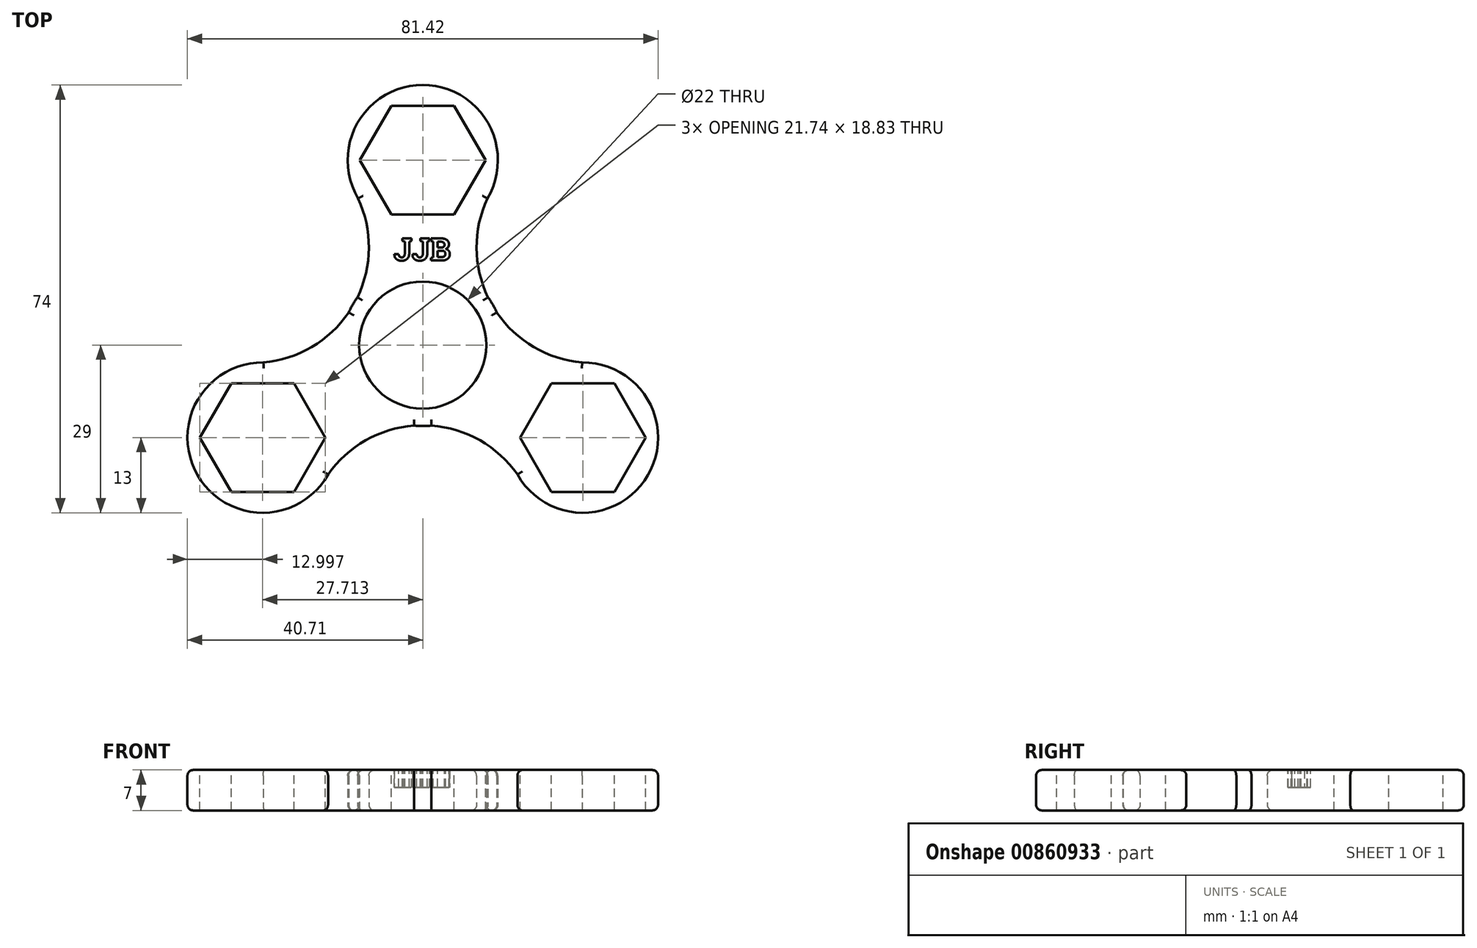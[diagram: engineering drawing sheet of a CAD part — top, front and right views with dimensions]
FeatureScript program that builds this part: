
annotation { "Feature Type Name" : "Feature", "Feature Type Description" : "" }
export const myFeature = defineFeature(function(context is Context, id is Id, definition is map)
    precondition{}
    {
        {
            var Q0;
            Q0=qCreatedBy(makeId("Top.planeOp"),FACE);
            var sketch = newSketch(context, id + "F0", { "sketchPlane" : qUnion([Q0])});
            skCircle(sketch, "E0", {"center": v(0, 0) * mm, "radius": 11 * mm});
            skCircle(sketch, "E1.0", {"center": v(0, 0) * mm, "radius": 14 * mm});
            skCircle(sketch, "E2", {"center": v(0, 0) * mm, "radius": 45 * mm, "construction": true});
            skArc(sketch, "E3", {"start": v(11.19, 25.38) * mm, "mid": v(0, 45) * mm, "end": v(-11.19, 25.38) * mm});
            skArc(sketch, "E4", {"start": v(-11.3, 8.27) * mm, "mid": v(-9.32, 16.81) * mm, "end": v(-11.19, 25.38) * mm});
            skArc(sketch, "E5.MirrorCS", {"start": v(11.3, 8.27) * mm, "mid": v(9.32, 16.81) * mm, "end": v(11.19, 25.38) * mm});
            skArc(sketch, "E6.1.0", {"start": v(-27.57, -3) * mm, "mid": v(-38.97, -22.5) * mm, "end": v(-16.39, -22.38) * mm});
            skArc(sketch, "E6.1.1", {"start": v(-1.52, -13.92) * mm, "mid": v(-9.9, -16.48) * mm, "end": v(-16.39, -22.38) * mm});
            skArc(sketch, "E6.1.2", {"start": v(-12.81, 5.65) * mm, "mid": v(-19.22, -0.34) * mm, "end": v(-27.57, -3) * mm});
            skArc(sketch, "E6.2.0", {"start": v(16.39, -22.38) * mm, "mid": v(38.97, -22.5) * mm, "end": v(27.57, -3) * mm});
            skArc(sketch, "E6.2.1", {"start": v(12.81, 5.65) * mm, "mid": v(19.22, -0.34) * mm, "end": v(27.57, -3) * mm});
            skArc(sketch, "E6.2.2", {"start": v(1.52, -13.92) * mm, "mid": v(9.9, -16.48) * mm, "end": v(16.39, -22.38) * mm});
            skText(sketch, "E7", { "text": "JJB", "fontName": "RobotoSlab-Bold.ttf"});
            const initialGuessF0  = {"E7": [-0.005, 0.0162, 1, 0, 0.00387]};
            skSetInitialGuess(sketch, initialGuessF0);
            skSolve(sketch);
        }
        {
            var Q0;
            {var subQ0=sQuery(id+"F0.wireOp",EDGE,"E4");Q0=makeQuery(id+"F0.imprint","IMPRINT",FACE,{"disambiguationData":[TD([[makeQuery(id+"F0.imprint","IMPRINT",EDGE,{"derivedFrom":subQ0}),-1.0]])]});}
            var Q1;
            {var subQ0=sQuery(id+"F0.wireOp",EDGE,"E3");var subQ1=makeQuery(id+"F0.imprint","INTERSECT",VERTEX,{"derivedFrom":[subQ0,sQuery(id+"F0.wireOp",EDGE,"E4")]});Q1=makeQuery(id+"F0.imprint","IMPRINT",FACE,{"disambiguationData":[TD([[makeQuery(id+"F0.imprint","IMPRINT",EDGE,{"disambiguationData":[TD([[subQ1,-1.0]])],"derivedFrom":subQ0}),1.0]])]});}
            var Q2;
            Q2=makeQuery(id+"F0.imprint","IMPRINT",FACE,{"disambiguationData":[TD([[makeQuery(id+"F0.imprint","IMPRINT",EDGE,{"derivedFrom":sQuery(id+"F0.wireOp",EDGE,"E0")}),-1.0]])]});
            var Q3;
            {var subQ0=sQuery(id+"F0.wireOp",EDGE,"E6.2.1");Q3=makeQuery(id+"F0.imprint","IMPRINT",FACE,{"disambiguationData":[TD([[makeQuery(id+"F0.imprint","IMPRINT",EDGE,{"derivedFrom":subQ0}),-1.0]])]});}
            var Q4;
            {var subQ0=sQuery(id+"F0.wireOp",EDGE,"E6.1.1");Q4=makeQuery(id+"F0.imprint","IMPRINT",FACE,{"disambiguationData":[TD([[makeQuery(id+"F0.imprint","IMPRINT",EDGE,{"derivedFrom":subQ0}),-1.0]])]});}
            var Q5;
            {var subQ0=sQuery(id+"F0.wireOp",EDGE,"E6.1.0");var subQ1=makeQuery(id+"F0.imprint","INTERSECT",VERTEX,{"derivedFrom":[subQ0,sQuery(id+"F0.wireOp",EDGE,"E6.1.1")]});Q5=makeQuery(id+"F0.imprint","IMPRINT",FACE,{"disambiguationData":[TD([[makeQuery(id+"F0.imprint","IMPRINT",EDGE,{"disambiguationData":[TD([[subQ1,-1.0]])],"derivedFrom":subQ0}),1.0]])]});}
            var Q6;
            {var subQ0=sQuery(id+"F0.wireOp",EDGE,"E6.2.0");var subQ1=makeQuery(id+"F0.imprint","INTERSECT",VERTEX,{"derivedFrom":[subQ0,sQuery(id+"F0.wireOp",EDGE,"E6.2.1")]});Q6=makeQuery(id+"F0.imprint","IMPRINT",FACE,{"disambiguationData":[TD([[makeQuery(id+"F0.imprint","IMPRINT",EDGE,{"disambiguationData":[TD([[subQ1,-1.0]])],"derivedFrom":subQ0}),1.0]])]});}
            var Q7;
            Q7=makeQuery(id+"F0.imprint","IMPRINT",FACE,{"disambiguationData":[TD([[makeQuery(id+"F0.imprint","IMPRINT",EDGE,{"derivedFrom":sQuery(id+"F0.wireOp",EDGE,"E7.sketch_text.stroke-36")}),-1.0]])]});
            var Q8;
            Q8=makeQuery(id+"F0.imprint","IMPRINT",FACE,{"disambiguationData":[TD([[makeQuery(id+"F0.imprint","IMPRINT",EDGE,{"derivedFrom":sQuery(id+"F0.wireOp",EDGE,"E7.sketch_text.stroke-18")}),-1.0]])]});
            var Q9;
            Q9=makeQuery(id+"F0.imprint","IMPRINT",FACE,{"disambiguationData":[TD([[makeQuery(id+"F0.imprint","IMPRINT",EDGE,{"derivedFrom":sQuery(id+"F0.wireOp",EDGE,"E7.sketch_text.stroke-0")}),-1.0]])]});
            var Q10;
            Q10=makeQuery(id+"F0.imprint","IMPRINT",FACE,{"disambiguationData":[TD([[makeQuery(id+"F0.imprint","IMPRINT",EDGE,{"derivedFrom":sQuery(id+"F0.wireOp",EDGE,"E7.sketch_text.stroke-59")}),1.0]])]});
            var Q11;
            Q11=makeQuery(id+"F0.imprint","IMPRINT",FACE,{"disambiguationData":[TD([[makeQuery(id+"F0.imprint","IMPRINT",EDGE,{"derivedFrom":sQuery(id+"F0.wireOp",EDGE,"E7.sketch_text.stroke-52")}),1.0]])]});
            extrude(context, id + "F1", {"entities" : qUnion([Q0, Q1, Q2, Q3, Q4, Q5, Q6, Q7, Q8, Q9, Q10, Q11]), "depth" : 7 * mm, "offsetDistance" : 25 * mm});
        }
        {
            var Q0;
            Q0=makeQuery(id+"F1.opExtrude","CAP_FACE",FACE,{"disambiguationData":[OSD([sQuery(id+"F0.wireOp",EDGE,"E0"),sQuery(id+"F0.wireOp",EDGE,"E1.0"),sQuery(id+"F0.wireOp",EDGE,"E3"),sQuery(id+"F0.wireOp",EDGE,"E4"),sQuery(id+"F0.wireOp",EDGE,"E5.MirrorCS"),sQuery(id+"F0.wireOp",EDGE,"E6.1.0"),sQuery(id+"F0.wireOp",EDGE,"E6.1.1"),sQuery(id+"F0.wireOp",EDGE,"E6.1.2"),sQuery(id+"F0.wireOp",EDGE,"E6.2.0"),sQuery(id+"F0.wireOp",EDGE,"E6.2.1"),sQuery(id+"F0.wireOp",EDGE,"E6.2.2")])],"isStart":true});
            var Q1;
            Q1=makeQuery(id+"F1.opExtrude","CAP_FACE",FACE,{"disambiguationData":[OSD([sQuery(id+"F0.wireOp",EDGE,"E0"),sQuery(id+"F0.wireOp",EDGE,"E1.0"),sQuery(id+"F0.wireOp",EDGE,"E3"),sQuery(id+"F0.wireOp",EDGE,"E4"),sQuery(id+"F0.wireOp",EDGE,"E5.MirrorCS"),sQuery(id+"F0.wireOp",EDGE,"E6.1.0"),sQuery(id+"F0.wireOp",EDGE,"E6.1.1"),sQuery(id+"F0.wireOp",EDGE,"E6.1.2"),sQuery(id+"F0.wireOp",EDGE,"E6.2.0"),sQuery(id+"F0.wireOp",EDGE,"E6.2.1"),sQuery(id+"F0.wireOp",EDGE,"E6.2.2")])],"isStart":false});
            fillet(context, id + "F2", {"entities" : qUnion([Q0, Q1]), "radius" : 1 * mm, "tangentPropagation" : true, "allowEdgeOverflow" : false});
        }
        {
            var Q0;
            Q0=makeQuery(id+"F1.opExtrude","CAP_FACE",FACE,{"disambiguationData":[OSD([sQuery(id+"F0.wireOp",EDGE,"E0"),sQuery(id+"F0.wireOp",EDGE,"E1.0"),sQuery(id+"F0.wireOp",EDGE,"E3"),sQuery(id+"F0.wireOp",EDGE,"E4"),sQuery(id+"F0.wireOp",EDGE,"E5.MirrorCS"),sQuery(id+"F0.wireOp",EDGE,"E6.1.0"),sQuery(id+"F0.wireOp",EDGE,"E6.1.1"),sQuery(id+"F0.wireOp",EDGE,"E6.1.2"),sQuery(id+"F0.wireOp",EDGE,"E6.2.0"),sQuery(id+"F0.wireOp",EDGE,"E6.2.1"),sQuery(id+"F0.wireOp",EDGE,"E6.2.2")])],"isStart":false});
            var sketch = newSketch(context, id + "F3", { "sketchPlane" : qUnion([Q0])});
            skCircle(sketch, "E8.cCircle", {"center": v(0, 32) * mm, "radius": 9.41 * mm, "construction": true});
            skLineSegment(sketch, "E8.0", {"start": v(5.44, 22.59) * mm, "end": v(-5.44, 22.59) * mm});
            skLineSegment(sketch, "E8.1", {"start": v(-5.44, 22.59) * mm, "end": v(-10.87, 32) * mm});
            skLineSegment(sketch, "E8.2", {"start": v(-10.87, 32) * mm, "end": v(-5.44, 41.41) * mm});
            skLineSegment(sketch, "E8.3", {"start": v(-5.44, 41.41) * mm, "end": v(5.44, 41.41) * mm});
            skLineSegment(sketch, "E8.4", {"start": v(5.44, 41.42) * mm, "end": v(10.87, 32) * mm});
            skLineSegment(sketch, "E8.5", {"start": v(10.87, 32) * mm, "end": v(5.44, 22.59) * mm});
            skPoint(sketch, "E8.0.midPoint", {"position": v(0, 22.59) * mm});
            skLineSegment(sketch, "E9.1.0", {"start": v(-33.15, -6.58) * mm, "end": v(-22.28, -6.58) * mm});
            skLineSegment(sketch, "E9.1.1", {"start": v(-22.28, -6.58) * mm, "end": v(-16.84, -16) * mm});
            skLineSegment(sketch, "E9.1.2", {"start": v(-16.84, -16) * mm, "end": v(-22.28, -25.41) * mm});
            skLineSegment(sketch, "E9.1.3", {"start": v(-22.28, -25.41) * mm, "end": v(-33.15, -25.41) * mm});
            skLineSegment(sketch, "E9.1.4", {"start": v(-33.15, -25.41) * mm, "end": v(-38.58, -16) * mm});
            skLineSegment(sketch, "E9.1.5", {"start": v(-38.58, -16) * mm, "end": v(-33.15, -6.58) * mm});
            skCircle(sketch, "E9.1.6", {"center": v(-27.71, -16) * mm, "radius": 9.41 * mm, "construction": true});
            skLineSegment(sketch, "E9.2.0", {"start": v(22.28, -25.42) * mm, "end": v(16.84, -16) * mm});
            skLineSegment(sketch, "E9.2.1", {"start": v(16.84, -16) * mm, "end": v(22.28, -6.59) * mm});
            skLineSegment(sketch, "E9.2.2", {"start": v(22.28, -6.59) * mm, "end": v(33.15, -6.59) * mm});
            skLineSegment(sketch, "E9.2.3", {"start": v(33.15, -6.59) * mm, "end": v(38.58, -16) * mm});
            skLineSegment(sketch, "E9.2.4", {"start": v(38.58, -16) * mm, "end": v(33.15, -25.42) * mm});
            skLineSegment(sketch, "E9.2.5", {"start": v(33.15, -25.42) * mm, "end": v(22.28, -25.42) * mm});
            skCircle(sketch, "E9.2.6", {"center": v(27.71, -16) * mm, "radius": 9.41 * mm, "construction": true});
            skPoint(sketch, "E9.center", {"position": v(0, 0) * mm});
            skSolve(sketch);
        }
        {
            var Q0;
            Q0=makeQuery(id+"F3.imprint","IMPRINT",FACE,{"disambiguationData":[TD([[makeQuery(id+"F3.imprint","IMPRINT",EDGE,{"derivedFrom":sQuery(id+"F3.wireOp",EDGE,"E8.0")}),-1.0]])]});
            var Q1;
            Q1=makeQuery(id+"F3.imprint","IMPRINT",FACE,{"disambiguationData":[TD([[makeQuery(id+"F3.imprint","IMPRINT",EDGE,{"derivedFrom":sQuery(id+"F3.wireOp",EDGE,"E9.1.0")}),-1.0]])]});
            var Q2;
            Q2=makeQuery(id+"F3.imprint","IMPRINT",FACE,{"disambiguationData":[TD([[makeQuery(id+"F3.imprint","IMPRINT",EDGE,{"derivedFrom":sQuery(id+"F3.wireOp",EDGE,"E9.2.0")}),-1.0]])]});
            extrude(context, id + "F4", {"entities" : qUnion([Q0, Q1, Q2]), "operationType" : NewBodyOperationType.REMOVE, "oppositeDirection" : true, "depth" : 25 * mm, "offsetDistance" : 25 * mm});
        }
        {
            var Q0;
            Q0=makeQuery(id+"F1.opExtrude","CAP_FACE",FACE,{"disambiguationData":[OSD([sQuery(id+"F0.wireOp",EDGE,"E0"),sQuery(id+"F0.wireOp",EDGE,"E1.0"),sQuery(id+"F0.wireOp",EDGE,"E3"),sQuery(id+"F0.wireOp",EDGE,"E4"),sQuery(id+"F0.wireOp",EDGE,"E5.MirrorCS"),sQuery(id+"F0.wireOp",EDGE,"E6.1.0"),sQuery(id+"F0.wireOp",EDGE,"E6.1.1"),sQuery(id+"F0.wireOp",EDGE,"E6.1.2"),sQuery(id+"F0.wireOp",EDGE,"E6.2.0"),sQuery(id+"F0.wireOp",EDGE,"E6.2.1"),sQuery(id+"F0.wireOp",EDGE,"E6.2.2")])],"isStart":false});
            var sketch = newSketch(context, id + "F5", { "sketchPlane" : qUnion([Q0])});
            skText(sketch, "E10", { "text": "JJB", "fontName": "RobotoSlab-Bold.ttf"});
            const initialGuessF5  = {"E10": [-0.005, 0.01465, 1, 0, 0.00387]};
            skSetInitialGuess(sketch, initialGuessF5);
            skSolve(sketch);
        }
        {
            var Q0;
            Q0=makeQuery(id+"F5.imprint","IMPRINT",FACE,{"disambiguationData":[TD([[makeQuery(id+"F5.imprint","IMPRINT",EDGE,{"derivedFrom":sQuery(id+"F5.wireOp",EDGE,"E10.sketch_text.stroke-0")}),-1.0]])]});
            var Q1;
            Q1=makeQuery(id+"F5.imprint","IMPRINT",FACE,{"disambiguationData":[TD([[makeQuery(id+"F5.imprint","IMPRINT",EDGE,{"derivedFrom":sQuery(id+"F5.wireOp",EDGE,"E10.sketch_text.stroke-18")}),-1.0]])]});
            var Q2;
            Q2=makeQuery(id+"F5.imprint","IMPRINT",FACE,{"disambiguationData":[TD([[makeQuery(id+"F5.imprint","IMPRINT",EDGE,{"derivedFrom":sQuery(id+"F5.wireOp",EDGE,"E10.sketch_text.stroke-36")}),-1.0]])]});
            extrude(context, id + "F6", {"entities" : qUnion([Q0, Q1, Q2]), "operationType" : NewBodyOperationType.REMOVE, "oppositeDirection" : true, "depth" : 3 * mm, "offsetDistance" : 25 * mm});
        }
    });
